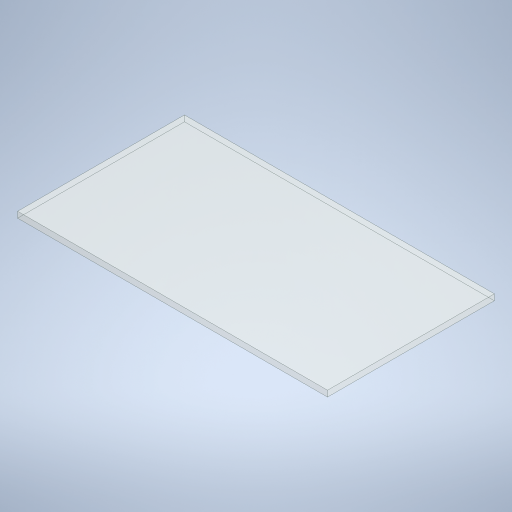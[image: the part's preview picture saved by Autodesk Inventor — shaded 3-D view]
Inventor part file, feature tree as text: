
AUTODESK INVENTOR PART (.ipt)
format: ipt  version: 2024 (Build 280153000, 153)  size: 223,232 bytes
history: native  units: in
note: dims shown in document units (in); Inventor stores cm internally (conversion verified against a paired STEP export)
features: extrude x1, sketch x1
ambient origin geometry x8: Origin, YZ Plane, XZ Plane, XY Plane, X Axis, Y Axis, Z Axis, Center Point
bodies: Solid1 (feature_tree)
feature tree (2):
  extrude  "Extrusion1"  Depth=7.0in
  sketch  "Sketch1"  dims[d0=13.0in d1=7.0in d2=0.25in d3=0.0in]
